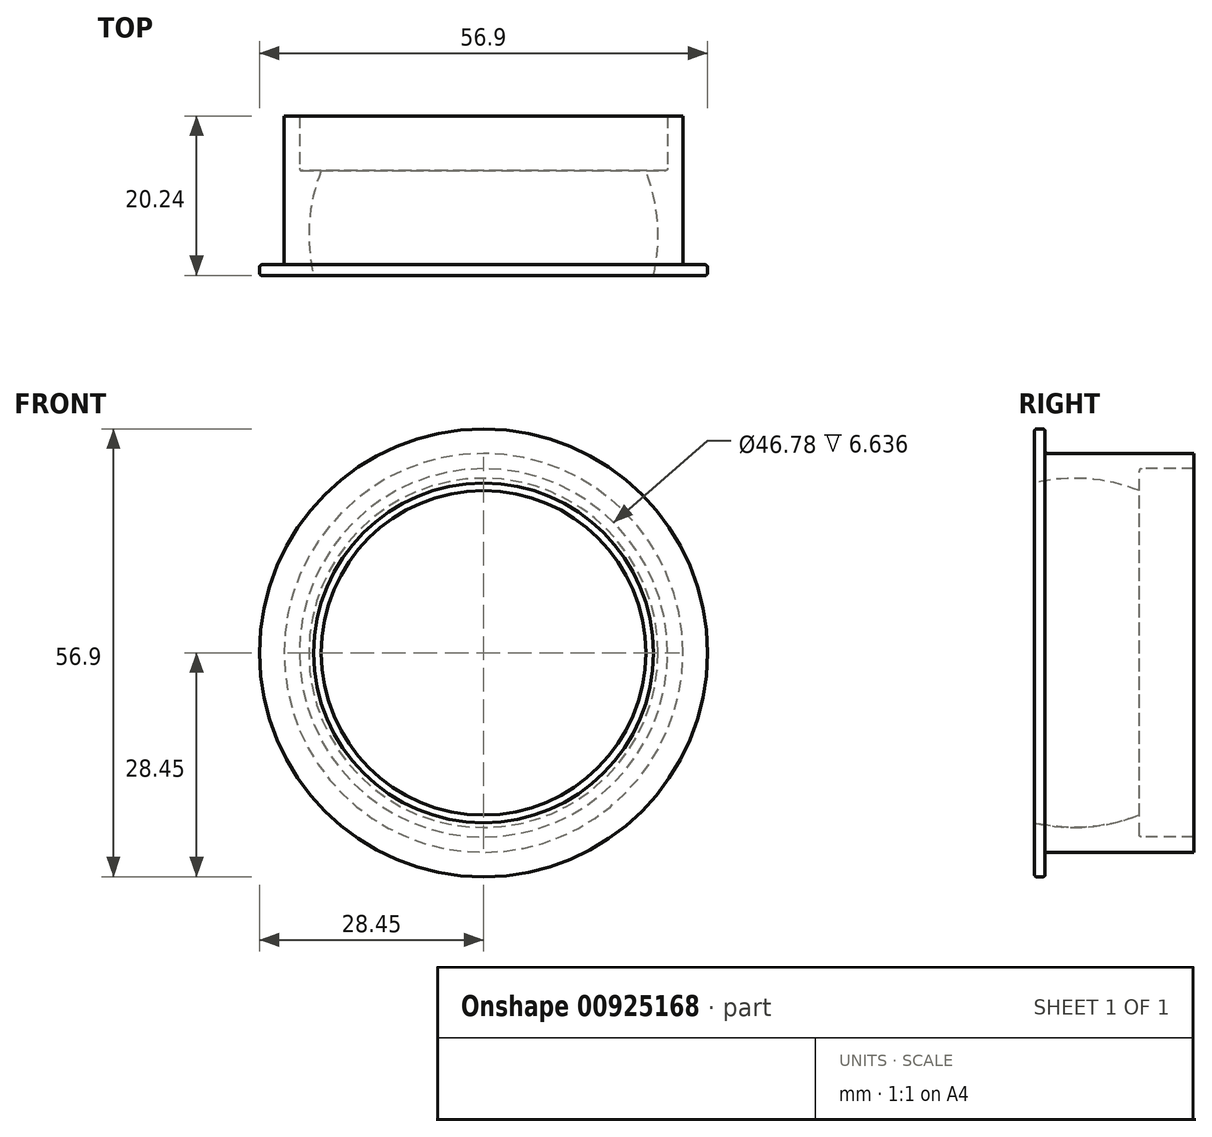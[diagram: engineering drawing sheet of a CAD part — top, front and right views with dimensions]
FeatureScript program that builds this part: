
annotation { "Feature Type Name" : "Feature", "Feature Type Description" : "" }
export const myFeature = defineFeature(function(context is Context, id is Id, definition is map)
    precondition{}
    {
        {
            var Q0;
            Q0=qCreatedBy(makeId("Right.planeOp"),FACE);
            var sketch = newSketch(context, id + "F0", { "sketchPlane" : qUnion([Q0])});
            skArc(sketch, "E0", {"start": v(-5.1, 21.58) * mm, "mid": v(1.62, 22.12) * mm, "end": v(8.2, 20.61) * mm});
            skLineSegment(sketch, "E1", {"start": v(-5.11, 21.58) * mm, "end": v(-5.11, 28.15) * mm});
            skLineSegment(sketch, "E2", {"start": v(-4.81, 28.45) * mm, "end": v(-4.06, 28.45) * mm});
            skLineSegment(sketch, "E3", {"start": v(-3.76, 28.15) * mm, "end": v(-3.76, 25.63) * mm});
            skLineSegment(sketch, "E4", {"start": v(-3.46, 25.33) * mm, "end": v(15.13, 25.33) * mm});
            skLineSegment(sketch, "E5", {"start": v(15.13, 25.33) * mm, "end": v(15.13, 23.4) * mm});
            skLineSegment(sketch, "E6", {"start": v(15.13, 23.4) * mm, "end": v(8.5, 23.4) * mm});
            skLineSegment(sketch, "E7", {"start": v(8.2, 23.09) * mm, "end": v(8.2, 20.61) * mm});
            skPoint(sketch, "E8.visualSharp", {"position": v(-5.11, 28.45) * mm});
            skArc(sketch, "E8.filletArc", {"start": v(-4.81, 28.45) * mm, "mid": v(-5.02, 28.36) * mm, "end": v(-5.11, 28.15) * mm});
            skPoint(sketch, "E9.visualSharp", {"position": v(-3.76, 28.45) * mm});
            skArc(sketch, "E9.filletArc", {"start": v(-3.76, 28.15) * mm, "mid": v(-3.85, 28.36) * mm, "end": v(-4.06, 28.45) * mm});
            skPoint(sketch, "E10.visualSharp", {"position": v(-3.76, 25.33) * mm});
            skArc(sketch, "E10.filletArc", {"start": v(-3.76, 25.63) * mm, "mid": v(-3.67, 25.42) * mm, "end": v(-3.46, 25.33) * mm});
            skPoint(sketch, "E11.visualSharp", {"position": v(8.2, 23.4) * mm});
            skArc(sketch, "E11.filletArc", {"start": v(8.5, 23.4) * mm, "mid": v(8.28, 23.3) * mm, "end": v(8.2, 23.09) * mm});
            skPoint(sketch, "E12.orphan", {"position": v(-22.18, 0) * mm});
            skPoint(sketch, "E13.orphan", {"position": v(22.18, 0) * mm});
            skLineSegment(sketch, "E14", {"start": v(-51.15, 0) * mm, "end": v(58.37, 0) * mm, "construction": true});
            skSolve(sketch);
        }
        {
            var Q0;
            Q0 = qSketchRegion(id + "F0", true);
            var Q1;
            Q1=sQuery(id+"F0.wireOp",EDGE,"E14");
            revolve(context, id + "F1", {"surfaceOperationType" : NewSurfaceOperationType.NEW, "entities" : qUnion([Q0]), "axis" : qUnion([Q1]), "revolveType" : RevolveType.FULL});
        }
    });
